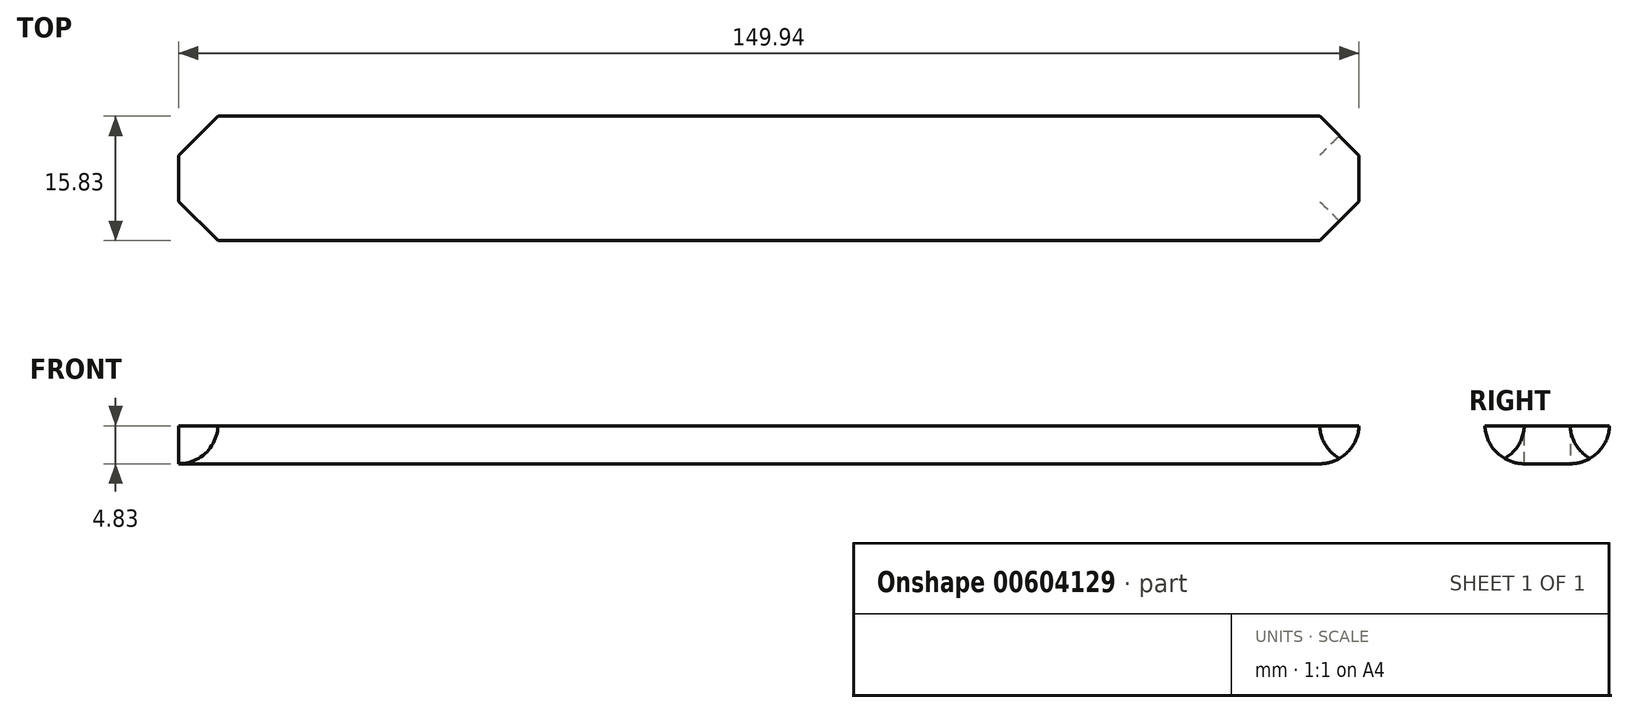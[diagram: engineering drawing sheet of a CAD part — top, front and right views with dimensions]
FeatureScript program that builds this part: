
annotation { "Feature Type Name" : "Feature", "Feature Type Description" : "" }
export const myFeature = defineFeature(function(context is Context, id is Id, definition is map)
    precondition{}
    {
        {
            var Q0;
            Q0=qCreatedBy(makeId("Top.planeOp"),FACE);
            var sketch = newSketch(context, id + "F0", { "sketchPlane" : qUnion([Q0])});
            skLineSegment(sketch, "E0.bottom", {"start": v(0, 0) * mm, "end": v(-149.94, 0) * mm});
            skLineSegment(sketch, "E0.top", {"start": v(0, 15.83) * mm, "end": v(-149.94, 15.83) * mm});
            skLineSegment(sketch, "E0.left", {"start": v(0, 0) * mm, "end": v(0, 15.83) * mm});
            skLineSegment(sketch, "E0.right", {"start": v(-149.94, 0) * mm, "end": v(-149.94, 15.83) * mm});
            skSolve(sketch);
        }
        {
            var Q0;
            Q0=makeQuery(id+"F0.imprint","IMPRINT",FACE,{"disambiguationData":[TD([[makeQuery(id+"F0.imprint","IMPRINT",EDGE,{"derivedFrom":sQuery(id+"F0.wireOp",EDGE,"E0.bottom")}),-1.0]])]});
            extrude(context, id + "F1", {"entities" : qUnion([Q0]), "depth" : 4.83 * mm, "offsetDistance" : 25.4 * mm});
        }
        {
            var Q0;
            Q0=makeQuery(id+"F1.opExtrude","SWEPT_EDGE",EDGE,{"disambiguationData":[OSD([sQuery(id+"F0.wireOp",EDGE,"E0.top"),sQuery(id+"F0.wireOp",EDGE,"E0.right")])]});
            var Q1;
            Q1=makeQuery(id+"F1.opExtrude","SWEPT_EDGE",EDGE,{"disambiguationData":[OSD([sQuery(id+"F0.wireOp",EDGE,"E0.bottom"),sQuery(id+"F0.wireOp",EDGE,"E0.right")])]});
            var Q2;
            Q2=makeQuery(id+"F1.opExtrude","SWEPT_EDGE",EDGE,{"disambiguationData":[OSD([sQuery(id+"F0.wireOp",EDGE,"E0.top"),sQuery(id+"F0.wireOp",EDGE,"E0.left")])]});
            var Q3;
            Q3=makeQuery(id+"F1.opExtrude","SWEPT_EDGE",EDGE,{"disambiguationData":[OSD([sQuery(id+"F0.wireOp",EDGE,"E0.bottom"),sQuery(id+"F0.wireOp",EDGE,"E0.left")])]});
            chamfer(context, id + "F2", {"entities" : qUnion([Q0, Q1, Q2, Q3]), "width" : 5 * mm, "tangentPropagation" : true});
        }
        {
            var Q0;
            Q0=makeQuery(id+"F1.opExtrude","CAP_EDGE",EDGE,{"disambiguationData":[OSD([sQuery(id+"F0.wireOp",EDGE,"E0.bottom")])],"isStart":true});
            fillet(context, id + "F3", {"entities" : qUnion([Q0]), "radius" : 5 * mm, "tangentPropagation" : true, "allowEdgeOverflow" : false});
        }
        {
            var Q0;
            Q0=makeQuery(id+"F1.opExtrude","CAP_EDGE",EDGE,{"disambiguationData":[OSD([sQuery(id+"F0.wireOp",EDGE,"E0.top")])],"isStart":true});
            fillet(context, id + "F4", {"entities" : qUnion([Q0]), "radius" : 5 * mm, "tangentPropagation" : true, "allowEdgeOverflow" : false});
        }
        {
            var Q0;
            Q0=makeQuery(id+"F1.opExtrude","CAP_EDGE",EDGE,{"disambiguationData":[OSD([sQuery(id+"F0.wireOp",EDGE,"E0.left")])],"isStart":true});
            fillet(context, id + "F5", {"entities" : qUnion([Q0]), "radius" : 5 * mm, "tangentPropagation" : true, "allowEdgeOverflow" : false});
        }
    });
